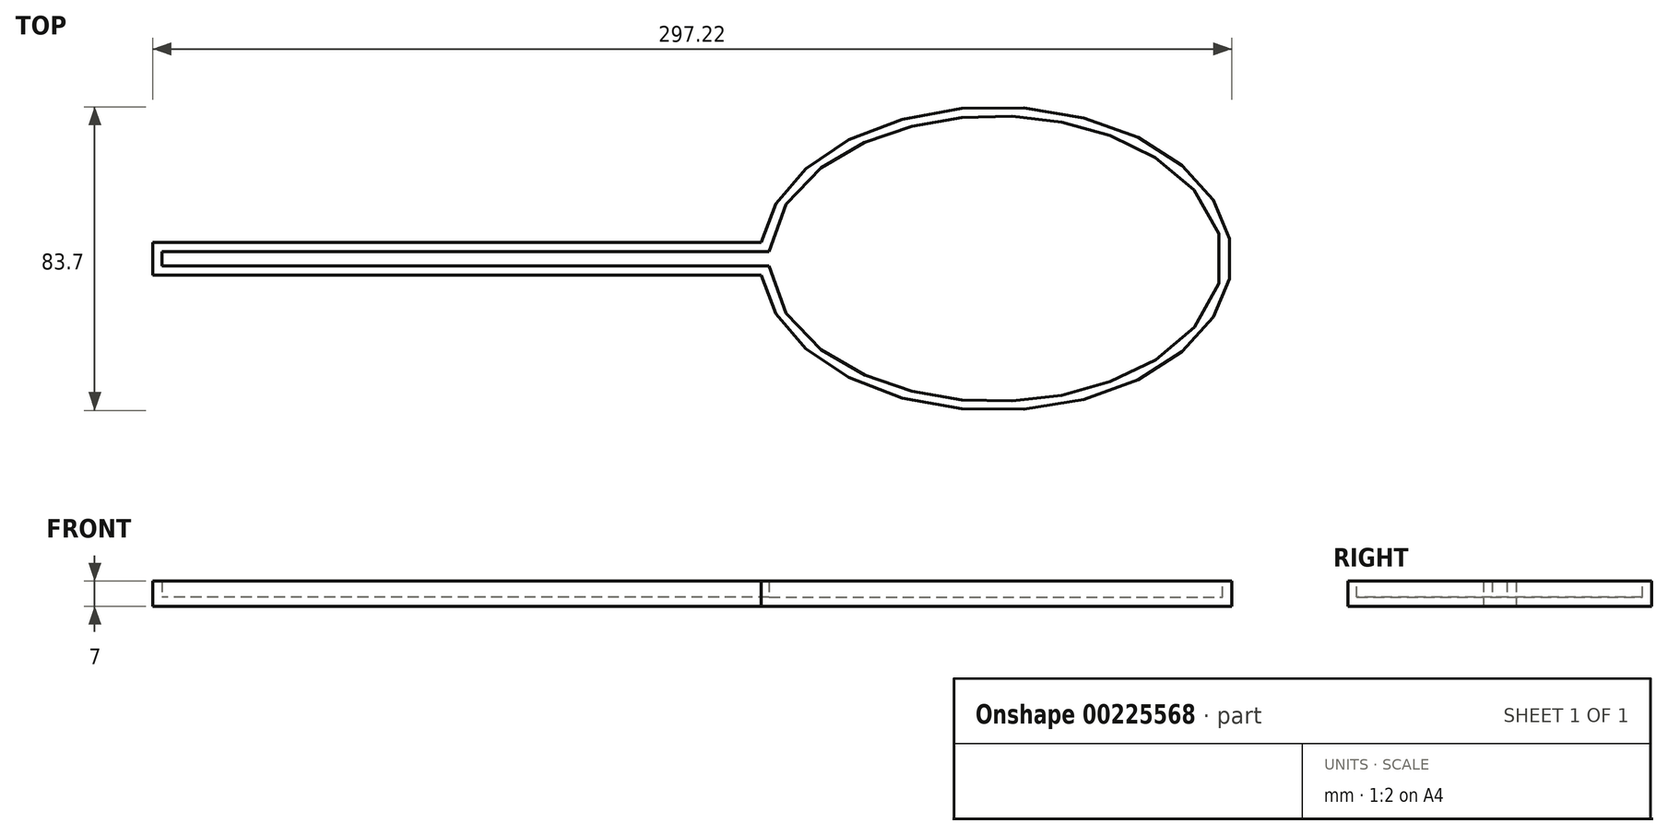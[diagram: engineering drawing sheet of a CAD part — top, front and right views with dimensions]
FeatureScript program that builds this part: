
annotation { "Feature Type Name" : "Feature", "Feature Type Description" : "" }
export const myFeature = defineFeature(function(context is Context, id is Id, definition is map)
    precondition{}
    {
        {
            var Q0;
            Q0=qCreatedBy(makeId("Top.planeOp"),FACE);
            var sketch = newSketch(context, id + "F0", { "sketchPlane" : qUnion([Q0])});
            skLineSegment(sketch, "E0.bottom", {"start": v(90, 4.5) * mm, "end": v(-90, 4.5) * mm});
            skLineSegment(sketch, "E0.top", {"start": v(90, -4.5) * mm, "end": v(-90, -4.5) * mm});
            skLineSegment(sketch, "E0.left", {"start": v(90, 4.5) * mm, "end": v(90, -4.5) * mm});
            skLineSegment(sketch, "E0.right", {"start": v(-90, 4.5) * mm, "end": v(-90, -4.5) * mm});
            skPoint(sketch, "E0.middle", {"position": v(0, 0) * mm});
            skEllipse(sketch, "E1", {"center": v(142.22, 0) * mm, "majorRadius": 65 * mm, "minorRadius": 41.85 * mm, "majorAxis": v(1, 0)});
            skSolve(sketch);
        }
        {
            var Q0;
            {var subQ0=sQuery(id+"F0.wireOp",EDGE,"E0.right");Q0=makeQuery(id+"F0.imprint","IMPRINT",FACE,{"disambiguationData":[TD([[makeQuery(id+"F0.imprint","IMPRINT",EDGE,{"derivedFrom":subQ0}),1.0]])]});}
            extrude(context, id + "F1", {"entities" : qUnion([Q0]), "depth" : 7 * mm});
        }
        {
            var Q0;
            {var subQ0=sQuery(id+"F0.wireOp",EDGE,"E0.left");Q0=makeQuery(id+"F0.imprint","IMPRINT",FACE,{"disambiguationData":[TD([[makeQuery(id+"F0.imprint","IMPRINT",EDGE,{"derivedFrom":subQ0}),1.0]])]});}
            var Q1;
            {var subQ0=sQuery(id+"F0.wireOp",EDGE,"E0.left");Q1=makeQuery(id+"F0.imprint","IMPRINT",FACE,{"disambiguationData":[TD([[makeQuery(id+"F0.imprint","IMPRINT",EDGE,{"derivedFrom":subQ0}),-1.0]])]});}
            extrude(context, id + "F2", {"entities" : qUnion([Q0, Q1]), "operationType" : NewBodyOperationType.ADD, "depth" : 7 * mm});
        }
        {
            var Q0;
            {var subQ0=sQuery(id+"F0.wireOp",EDGE,"E1");Q0=makeQuery(id+"F2.boolean.opBoolean","MERGE",FACE,{"derivedFrom":[makeQuery(id+"F1.opExtrude","CAP_FACE",FACE,{"disambiguationData":[OSD([sQuery(id+"F0.wireOp",EDGE,"E0.bottom"),sQuery(id+"F0.wireOp",EDGE,"E0.top"),sQuery(id+"F0.wireOp",EDGE,"E0.right"),subQ0])],"isStart":false}),makeQuery(id+"F2.opExtrude","CAP_FACE",FACE,{"disambiguationData":[OSD([subQ0])],"isStart":false})]});}
            shell(context, id + "F3", {"entities" : qUnion([Q0]), "thickness" : 2.5 * mm});
        }
    });
